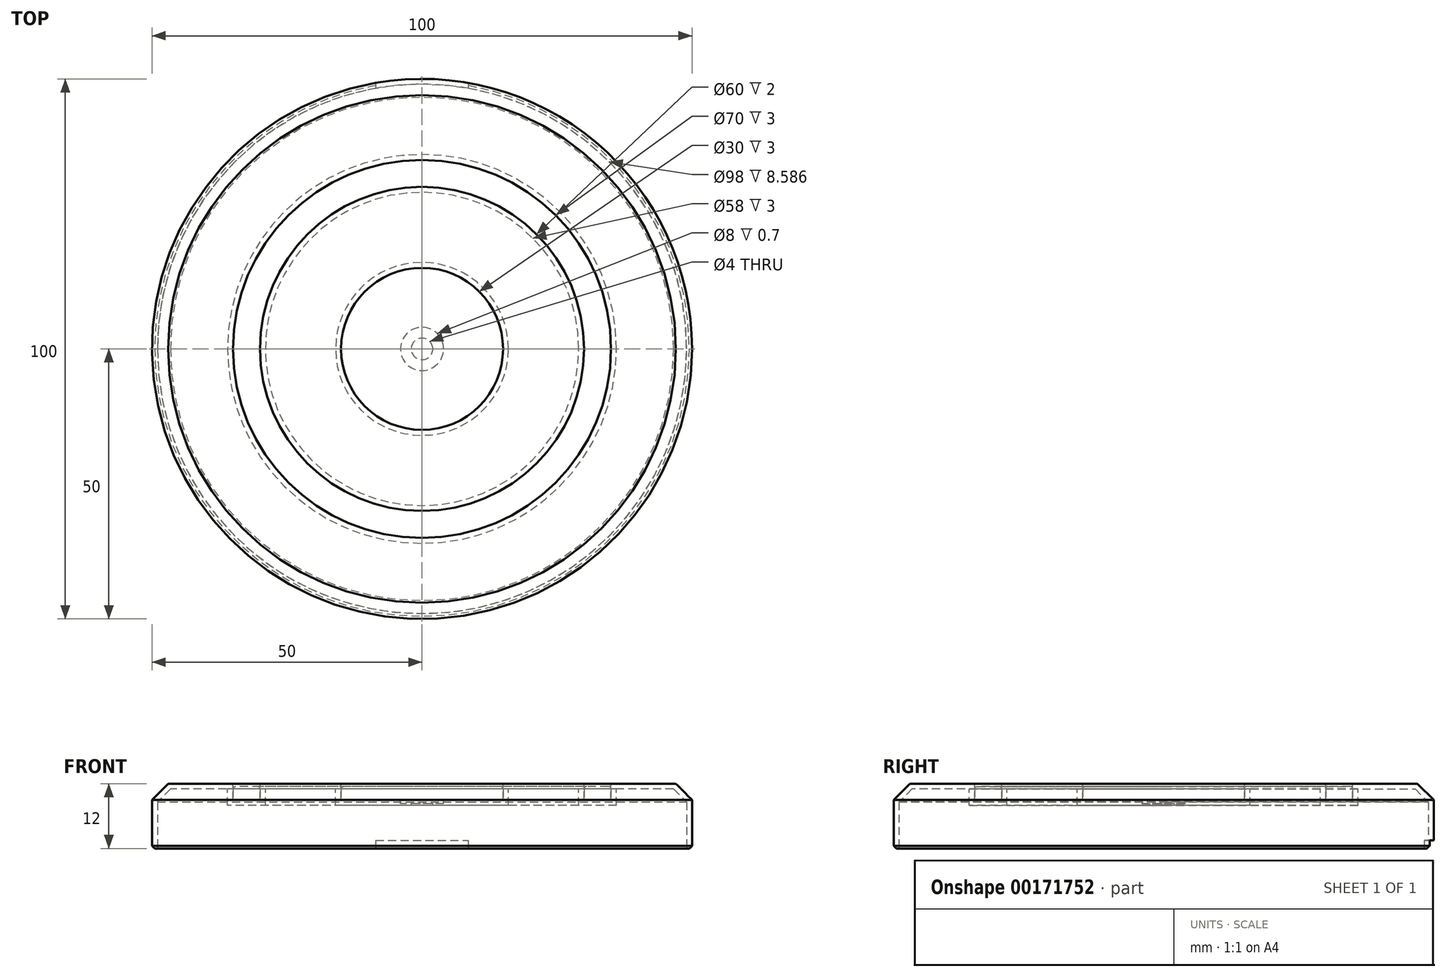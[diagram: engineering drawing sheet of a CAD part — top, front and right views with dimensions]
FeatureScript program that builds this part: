
annotation { "Feature Type Name" : "Feature", "Feature Type Description" : "" }
export const myFeature = defineFeature(function(context is Context, id is Id, definition is map)
    precondition{}
    {
        {
            var Q0;
            Q0=qCreatedBy(makeId("Top.planeOp"),FACE);
            var sketch = newSketch(context, id + "F0", { "sketchPlane" : qUnion([Q0])});
            skCircle(sketch, "E0", {"center": v(0, 0) * mm, "radius": 50 * mm});
            skSolve(sketch);
        }
        {
            var Q0;
            Q0 = qSketchRegion(id + "F0", true);
            extrude(context, id + "F1", {"entities" : qUnion([Q0]), "depth" : 12 * mm});
        }
        {
            var Q0;
            Q0=makeQuery(id+"F1.opExtrude","CAP_EDGE",EDGE,{"disambiguationData":[OSD([sQuery(id+"F0.wireOp",EDGE,"E0")])],"isStart":false});
            chamfer(context, id + "F2", {"entities" : qUnion([Q0]), "width" : 3 * mm, "tangentPropagation" : true});
        }
        {
            var Q0;
            Q0=makeQuery(id+"F1.opExtrude","CAP_EDGE",EDGE,{"disambiguationData":[OSD([sQuery(id+"F0.wireOp",EDGE,"E0")])],"isStart":true});
            chamfer(context, id + "F3", {"entities" : qUnion([Q0]), "width" : 0.5 * mm, "tangentPropagation" : true});
        }
        {
            var Q0;
            Q0=makeQuery(id+"F1.opExtrude","CAP_FACE",FACE,{"disambiguationData":[OSD([sQuery(id+"F0.wireOp",EDGE,"E0")])],"isStart":false});
            var sketch = newSketch(context, id + "F4", { "sketchPlane" : qUnion([Q0])});
            skCircle(sketch, "E1", {"center": v(0, 0) * mm, "radius": 35 * mm});
            skCircle(sketch, "E2", {"center": v(0, 0) * mm, "radius": 30 * mm});
            skCircle(sketch, "E3", {"center": v(0, 0) * mm, "radius": 15 * mm});
            skSolve(sketch);
        }
        {
            var Q0;
            Q0 = qSketchRegion(id + "F4", true);
            var Q1;
            Q1=makeQuery(id+"F4.imprint","IMPRINT",FACE,{"disambiguationData":[TD([[makeQuery(id+"F4.imprint","IMPRINT",EDGE,{"derivedFrom":sQuery(id+"F4.wireOp",EDGE,"E3")}),1.0]])]});
            extrude(context, id + "F5", {"entities" : qUnion([Q0, Q1]), "operationType" : NewBodyOperationType.REMOVE, "oppositeDirection" : true, "depth" : 3 * mm});
        }
        {
            var Q0;
            Q0=makeQuery(id+"F5.boolean.opBoolean","COPY",FACE,{"derivedFrom":makeQuery(id+"F5.opExtrude","CAP_FACE",FACE,{"disambiguationData":[OSD([sQuery(id+"F4.wireOp",EDGE,"E3")])],"isStart":false})});
            var sketch = newSketch(context, id + "F6", { "sketchPlane" : qUnion([Q0])});
            skCircle(sketch, "E4", {"center": v(0, 0) * mm, "radius": 35 * mm});
            skCircle(sketch, "E5", {"center": v(0, 0) * mm, "radius": 30 * mm});
            skCircle(sketch, "E6", {"center": v(0, 0) * mm, "radius": 15 * mm});
            skSolve(sketch);
        }
        {
            var Q0;
            Q0 = qSketchRegion(id + "F6", true);
            var Q1;
            Q1=makeQuery(id+"F6.imprint","IMPRINT",FACE,{"disambiguationData":[TD([[makeQuery(id+"F6.imprint","IMPRINT",EDGE,{"derivedFrom":sQuery(id+"F6.wireOp",EDGE,"E6")}),1.0]])]});
            extrude(context, id + "F7", {"entities" : qUnion([Q0, Q1]), "depth" : 2.5 * mm});
        }
        {
            var Q0;
            Q0=makeQuery(id+"F7.opExtrude","CAP_EDGE",EDGE,{"disambiguationData":[OSD([sQuery(id+"F6.wireOp",EDGE,"E4")])],"isStart":false});
            var Q1;
            Q1=makeQuery(id+"F7.opExtrude","CAP_EDGE",EDGE,{"disambiguationData":[OSD([sQuery(id+"F6.wireOp",EDGE,"E5")])],"isStart":false});
            fillet(context, id + "F8", {"entities" : qUnion([Q0, Q1]), "radius" : 0.5 * mm, "tangentPropagation" : true, "allowEdgeOverflow" : false});
        }
        {
            var Q0;
            Q0=makeQuery(id+"F7.opExtrude","CAP_EDGE",EDGE,{"disambiguationData":[OSD([sQuery(id+"F6.wireOp",EDGE,"E6")])],"isStart":false});
            fillet(context, id + "F9", {"entities" : qUnion([Q0]), "radius" : 0.5 * mm, "tangentPropagation" : true, "allowEdgeOverflow" : false});
        }
        {
            var Q0;
            Q0=makeQuery(id+"F1.opExtrude","CAP_FACE",FACE,{"disambiguationData":[OSD([sQuery(id+"F0.wireOp",EDGE,"E0")])],"isStart":true});
            shell(context, id + "F10", {"entities" : qUnion([Q0]), "thickness" : 1 * mm});
        }
        {
            var Q0;
            Q0=makeQuery(id+"F1.opExtrude","CAP_FACE",FACE,{"disambiguationData":[OSD([sQuery(id+"F0.wireOp",EDGE,"E0")])],"isStart":true});
            var sketch = newSketch(context, id + "F11", { "sketchPlane" : qUnion([Q0])});
            skLineSegment(sketch, "E7.bottom", {"start": v(8.58, -50.53) * mm, "end": v(-8.58, -50.53) * mm});
            skLineSegment(sketch, "E7.top", {"start": v(8.58, -47.03) * mm, "end": v(-8.58, -47.03) * mm});
            skLineSegment(sketch, "E7.left", {"start": v(8.58, -50.53) * mm, "end": v(8.58, -47.03) * mm});
            skLineSegment(sketch, "E7.right", {"start": v(-8.58, -50.53) * mm, "end": v(-8.58, -47.03) * mm});
            skPoint(sketch, "E7.middle", {"position": v(0, -48.78) * mm});
            skSolve(sketch);
        }
        {
            var Q0;
            Q0 = qSketchRegion(id + "F11", true);
            extrude(context, id + "F12", {"entities" : qUnion([Q0]), "operationType" : NewBodyOperationType.REMOVE, "oppositeDirection" : true, "depth" : 1.5 * mm});
        }
        {
            var Q0;
            Q0=makeQuery(id+"F5.boolean.opBoolean","COPY",FACE,{"derivedFrom":makeQuery(id+"F5.opExtrude","CAP_FACE",FACE,{"disambiguationData":[OSD([sQuery(id+"F4.wireOp",EDGE,"E3")])],"isStart":false})});
            var sketch = newSketch(context, id + "F13", { "sketchPlane" : qUnion([Q0])});
            skCircle(sketch, "E8", {"center": v(0, 0) * mm, "radius": 4 * mm});
            skSolve(sketch);
        }
        {
            var Q0;
            Q0=makeQuery(id+"F13.imprint","IMPRINT",FACE,{"disambiguationData":[TD([[makeQuery(id+"F13.imprint","IMPRINT",EDGE,{"derivedFrom":sQuery(id+"F13.wireOp",EDGE,"E8")}),1.0]])]});
            extrude(context, id + "F14", {"entities" : qUnion([Q0]), "operationType" : NewBodyOperationType.REMOVE, "oppositeDirection" : true, "depth" : 0.7 * mm});
        }
        {
            var Q0;
            Q0=makeQuery(id+"F14.boolean.opBoolean","COPY",FACE,{"derivedFrom":makeQuery(id+"F14.opExtrude","CAP_FACE",FACE,{"disambiguationData":[OSD([sQuery(id+"F13.wireOp",EDGE,"E8")])],"isStart":false})});
            var sketch = newSketch(context, id + "F15", { "sketchPlane" : qUnion([Q0])});
            skCircle(sketch, "E9", {"center": v(0, 0) * mm, "radius": 2 * mm});
            skSolve(sketch);
        }
        {
            var Q0;
            Q0=makeQuery(id+"F15.imprint","IMPRINT",FACE,{"disambiguationData":[TD([[makeQuery(id+"F15.imprint","IMPRINT",EDGE,{"derivedFrom":sQuery(id+"F15.wireOp",EDGE,"E9")}),1.0]])]});
            extrude(context, id + "F16", {"entities" : qUnion([Q0]), "operationType" : NewBodyOperationType.REMOVE, "endBound" : BoundingType.THROUGH_ALL, "oppositeDirection" : true, "depth" : 25 * mm});
        }
        {
            var Q0;
            Q0=qCreatedBy(makeId("Front.planeOp"),FACE);
            var sketch = newSketch(context, id + "F17", { "sketchPlane" : qUnion([Q0])});
            skLineSegment(sketch, "E10", {"start": v(0, 17.46) * mm, "end": v(0, -16.56) * mm, "construction": true});
            skSolve(sketch);
        }
        {
            var Q0;
            Q0=makeQuery(id+"F12.boolean.opBoolean","COPY",FACE,{"derivedFrom":makeQuery(id+"F12.opExtrude","SWEPT_FACE",FACE,{"disambiguationData":[OSD([sQuery(id+"F11.wireOp",EDGE,"E7.left")])]})});
            var sketch = newSketch(context, id + "F18", { "sketchPlane" : qUnion([Q0])});
            skLineSegment(sketch, "E11", {"start": v(-48.24, 0.91) * mm, "end": v(-48.24, 0) * mm});
            skLineSegment(sketch, "E12", {"start": v(-48.24, 0) * mm, "end": v(-47.31, 0) * mm});
            skLineSegment(sketch, "E13", {"start": v(-47.31, 0) * mm, "end": v(-48.24, 0.91) * mm});
            skSolve(sketch);
        }
        {
            var Q0;
            Q0 = qSketchRegion(id + "F18", true);
            var Q1;
            Q1=sQuery(id+"F17.wireOp",EDGE,"E10");
            revolve(context, id + "F19", {"operationType" : NewBodyOperationType.REMOVE, "entities" : qUnion([Q0]), "axis" : qUnion([Q1]), "revolveType" : RevolveType.FULL, "oppositeDirection" : true});
        }
    });
